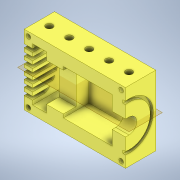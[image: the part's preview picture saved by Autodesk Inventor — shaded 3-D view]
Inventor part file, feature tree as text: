
AUTODESK INVENTOR PART (.ipt)
format: ipt  version: 2022.2 (Build 262287000, 287)  size: 358,400 bytes
history: native  units: mm
features: extrude x8, sketch x8, hole x4, mirror x1
ambient origin geometry x8: Origin, YZ Plane, XZ Plane, XY Plane, X Axis, Y Axis, Z Axis, Center Point
bodies: Solid1 (feature_tree)
feature tree (21):
  extrude  "MainInnerBodyExtrusion"  Depth=83.0mm
  extrude  "HoleForCameraCase"  Depth=15.7mm
  extrude  "HoleForFan"  Depth=58.0mm
  extrude  "SlotsForRearFan"  TaperAngle=0.0deg  [1 undecoded]
  extrude  "VentForCamera"  Depth=63.0mm
  extrude  "HoleForLens"  Depth=31.5mm
  hole  "Hole for 6-32 Insert"  [1 undecoded]
  hole  "Screw hole for 6-32 screw"  [1 undecoded]
  extrude  "HoleForLensCover"  Depth=4.0mm
  extrude  "Extrusion23"  Depth=4.0mm
  hole  "Hole7"  [1 undecoded]
  mirror  "Mirror4"
  sketch  "Sketch1"  dims[d0=120.2mm d1=83.0mm]
  sketch  "Sketch3"  dims[d2=36.0mm d3=0.0mm d5=15.7mm]
  sketch  "Sketch4"  dims[d6=53.0mm d7=58.0mm]
  sketch  "Sketch15"  dims[d8=30.375mm d9=0.0mm]
  sketch  "Sketch16"  dims[d13=16.5mm d14=63.0mm]
  sketch  "Sketch18"  dims[d15=10.0mm d16=31.5mm]
  hole  "HoleFor50mmLensCover"  [1 undecoded]
  sketch  "Sketch32"  dims[d17=0.0mm d67=60.0mm]
  sketch  "Sketch33"  dims[d69=2.0mm d71=4.0mm d72=4.0mm d73=4.0mm d75=4.0mm d76=10.0mm d77=0.0mm d78=15.5mm d79=22.0mm d89=1.5mm d90=3.0mm d91=3.0mm d92=3.0mm d93=0.0mm d94=0.0mm d95=17.5mm d97=18.5mm d98=20.0mm d99=0.0mm d106=5.0mm d108=5.0mm d109=4.7mm d110=6.0mm d111=5.54mm d112=5.55mm d113=90.0deg d114=7.2mm d115=20.594885mm d116=3.797mm d117=6.0mm d118=12.7mm d119=2.362mm d120=90.0deg d121=15.0mm d122=20.594885mm d137=4.125mm d142=30.0mm d163=56.0mm d164=49.0mm d165=3.0mm d166=0.0mm d179=0.0mm d180=4.0mm d181=4.0mm d182=15.0mm d183=0.0mm d184=11.82mm d185=50.0mm d187=23.64mm d188=10.0mm d190=10.0mm d192=6.756mm d193=6.0mm d194=8.15086mm d195=7.4168mm d196=14.3117mm d197=9.0mm d198=0.0mm d162=0.5mm]
note: 5 required parameter values undecoded (feature->parameter linkage not recoverable at this tier; creation-order binding heuristic only, values carry confidence <= 0.55)
